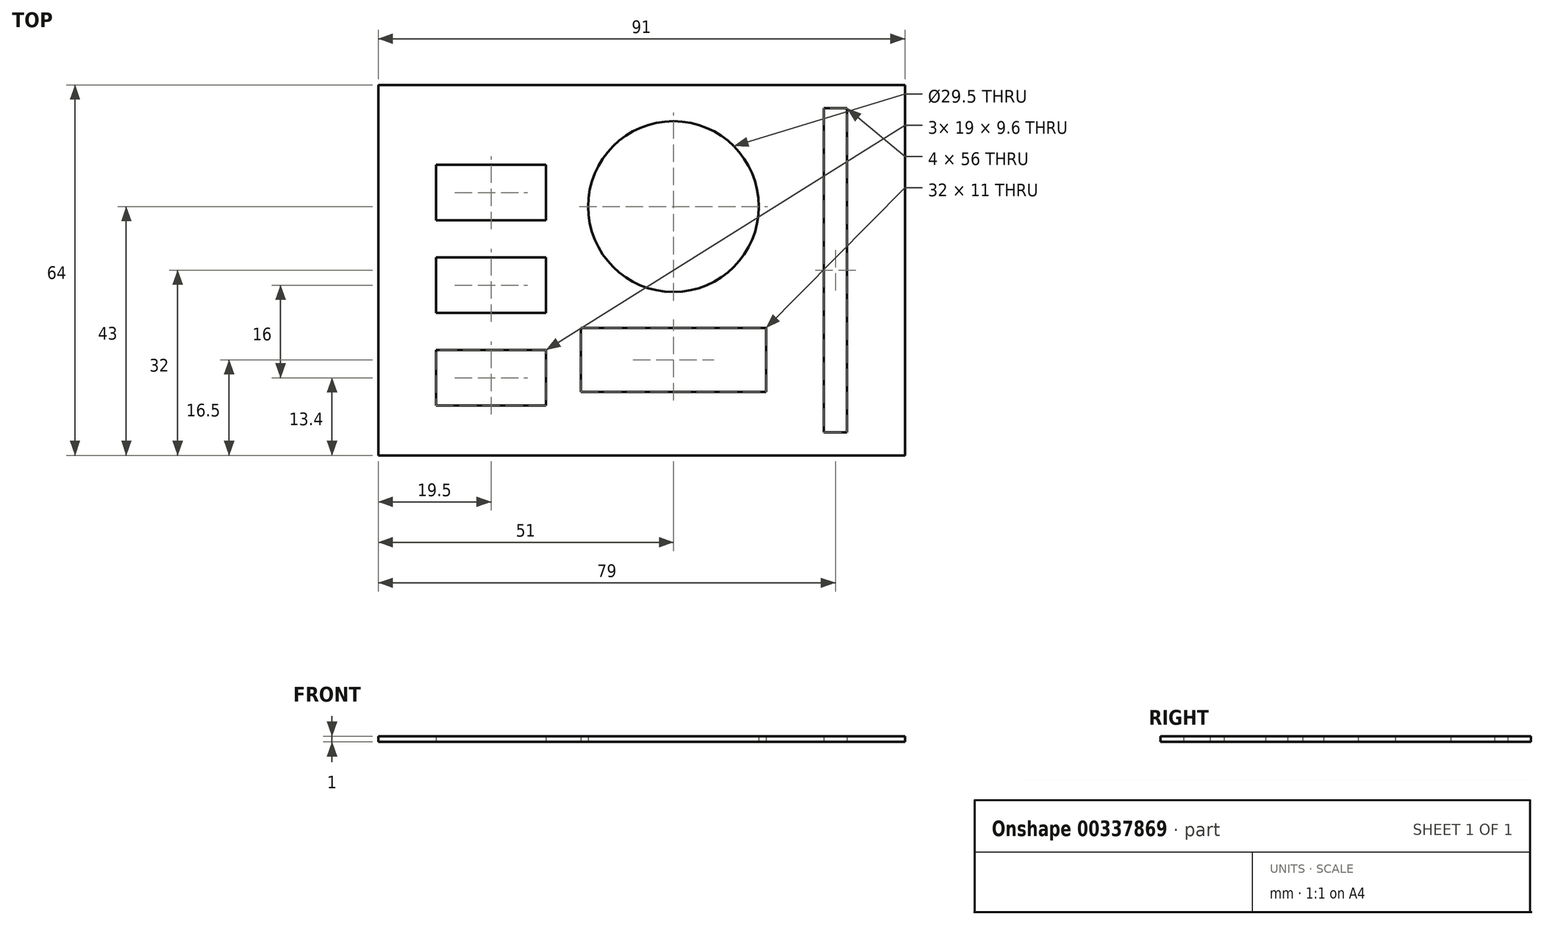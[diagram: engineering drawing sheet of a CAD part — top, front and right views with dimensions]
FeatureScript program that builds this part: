
annotation { "Feature Type Name" : "Feature", "Feature Type Description" : "" }
export const myFeature = defineFeature(function(context is Context, id is Id, definition is map)
    precondition{}
    {
        {
            var Q0;
            Q0=qCreatedBy(makeId("Top.planeOp"),FACE);
            var sketch = newSketch(context, id + "F0", { "sketchPlane" : qUnion([Q0])});
            skCircle(sketch, "E0", {"center": v(51, -21) * mm, "radius": 14.75 * mm});
            skLineSegment(sketch, "E1.bottom", {"start": v(0, -64) * mm, "end": v(91, -64) * mm});
            skLineSegment(sketch, "E1.top", {"start": v(0, 0) * mm, "end": v(91, 0) * mm});
            skLineSegment(sketch, "E1.left", {"start": v(0, -64) * mm, "end": v(0, 0) * mm});
            skLineSegment(sketch, "E1.right", {"start": v(91, -64) * mm, "end": v(91, 0) * mm});
            skLineSegment(sketch, "E2.bottom", {"start": v(77, -4) * mm, "end": v(81, -4) * mm});
            skLineSegment(sketch, "E2.top", {"start": v(77, -60) * mm, "end": v(81, -60) * mm});
            skLineSegment(sketch, "E2.left", {"start": v(77, -4) * mm, "end": v(77, -60) * mm});
            skLineSegment(sketch, "E2.right", {"start": v(81, -4) * mm, "end": v(81, -60) * mm});
            skLineSegment(sketch, "E3.bottom", {"start": v(35, -42) * mm, "end": v(67, -42) * mm});
            skLineSegment(sketch, "E3.top", {"start": v(35, -53) * mm, "end": v(67, -53) * mm});
            skLineSegment(sketch, "E3.left", {"start": v(35, -42) * mm, "end": v(35, -53) * mm});
            skLineSegment(sketch, "E3.right", {"start": v(67, -42) * mm, "end": v(67, -53) * mm});
            skPoint(sketch, "E4", {"position": v(51, -42) * mm});
            skLineSegment(sketch, "E5", {"start": v(51, -42) * mm, "end": v(51, 0) * mm, "construction": true});
            skLineSegment(sketch, "E6.bottom", {"start": v(10, -13.8) * mm, "end": v(29, -13.8) * mm});
            skLineSegment(sketch, "E6.top", {"start": v(10, -23.4) * mm, "end": v(29, -23.4) * mm});
            skLineSegment(sketch, "E6.left", {"start": v(10, -13.8) * mm, "end": v(10, -23.4) * mm});
            skLineSegment(sketch, "E6.right", {"start": v(29, -13.8) * mm, "end": v(29, -23.4) * mm});
            skLineSegment(sketch, "E7.bottom", {"start": v(10, -29.8) * mm, "end": v(29, -29.8) * mm});
            skLineSegment(sketch, "E7.top", {"start": v(10, -39.4) * mm, "end": v(29, -39.4) * mm});
            skLineSegment(sketch, "E7.left", {"start": v(10, -29.8) * mm, "end": v(10, -39.4) * mm});
            skLineSegment(sketch, "E7.right", {"start": v(29, -29.8) * mm, "end": v(29, -39.4) * mm});
            skLineSegment(sketch, "E8.bottom", {"start": v(10, -45.8) * mm, "end": v(29, -45.8) * mm});
            skLineSegment(sketch, "E8.top", {"start": v(10, -55.4) * mm, "end": v(29, -55.4) * mm});
            skLineSegment(sketch, "E8.left", {"start": v(10, -45.8) * mm, "end": v(10, -55.4) * mm});
            skLineSegment(sketch, "E8.right", {"start": v(29, -45.8) * mm, "end": v(29, -55.4) * mm});
            skLineSegment(sketch, "E9", {"start": v(10, 0) * mm, "end": v(10, -64) * mm, "construction": true});
            skSolve(sketch);
        }
        {
            var Q0;
            Q0=makeQuery(id+"F0.imprint","IMPRINT",FACE,{"disambiguationData":[TD([[makeQuery(id+"F0.imprint","IMPRINT",EDGE,{"derivedFrom":sQuery(id+"F0.wireOp",EDGE,"E0")}),1.0]])]});
            extrude(context, id + "F1", {"entities" : qUnion([Q0]), "depth" : 1 * mm});
        }
        {
            var Q0;
            Q0=qSketchRegion(id+"F0",true);
            extrude(context, id + "F2", {"entities" : qUnion([Q0]), "depth" : 1 * mm});
        }
    });
